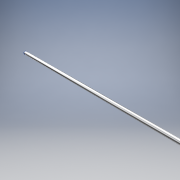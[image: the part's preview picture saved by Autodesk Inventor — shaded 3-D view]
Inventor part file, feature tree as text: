
AUTODESK INVENTOR PART (.ipt)
format: ipt  version: 2019 (Build 230136000, 136)  size: 92,160 bytes
history: native  units: in
note: dims shown in document units (in); Inventor stores cm internally (conversion verified against a paired STEP export)
features: extrude x1, sketch x1
ambient origin geometry x8: Origin, YZ Plane, XZ Plane, XY Plane, X Axis, Y Axis, Z Axis, Center Point
bodies: Solid1 (feature_tree)
feature tree (2):
  extrude  "Extrusion1"  Depth=24.0in TaperAngle=0.0deg
  sketch  "Sketch1"  dims[d0=0.5in d1=24.0in d2=0.0in]
